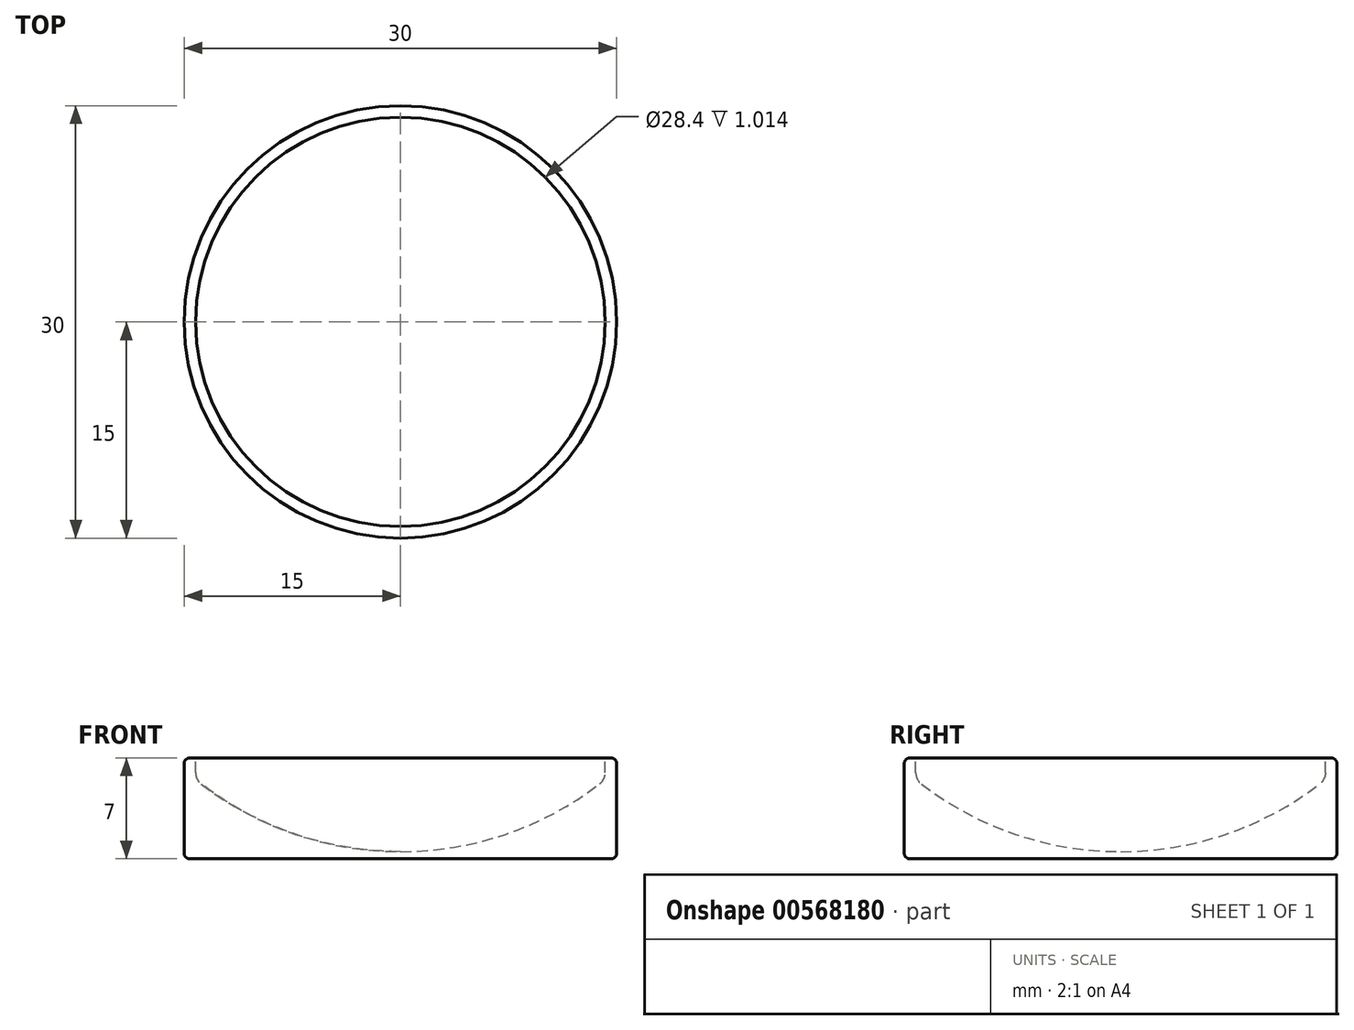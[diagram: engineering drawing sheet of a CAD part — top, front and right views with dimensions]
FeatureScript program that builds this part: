
annotation { "Feature Type Name" : "Feature", "Feature Type Description" : "" }
export const myFeature = defineFeature(function(context is Context, id is Id, definition is map)
    precondition{}
    {
        {
            var Q0;
            Q0=qCreatedBy(makeId("Front.planeOp"),FACE);
            var sketch = newSketch(context, id + "F0", { "sketchPlane" : qUnion([Q0])});
            skLineSegment(sketch, "E0", {"start": v(-15, 0) * mm, "end": v(-15, 7) * mm});
            skLineSegment(sketch, "E1", {"start": v(-15, 7) * mm, "end": v(-14.2, 7) * mm});
            skLineSegment(sketch, "E2", {"start": v(-14.2, 7) * mm, "end": v(-14.2, 5.5) * mm});
            skLineSegment(sketch, "E3", {"start": v(0, 0.5) * mm, "end": v(0, 0) * mm});
            skLineSegment(sketch, "E4", {"start": v(0, 0) * mm, "end": v(-15, 0) * mm});
            skArc(sketch, "E5", {"start": v(-14.2, 5.5) * mm, "mid": v(-7.53, 1.79) * mm, "end": v(0, 0.5) * mm});
            skSolve(sketch);
        }
        {
            var Q0;
            Q0=makeQuery(id+"F0.imprint","IMPRINT",FACE,{"disambiguationData":[TD([[makeQuery(id+"F0.imprint","IMPRINT",EDGE,{"derivedFrom":sQuery(id+"F0.wireOp",EDGE,"E0")}),-1.0]])]});
            var Q1;
            Q1=sQuery(id+"F0.wireOp",EDGE,"E3");
            revolve(context, id + "F1", {"entities" : qUnion([Q0]), "axis" : qUnion([Q1]), "revolveType" : RevolveType.FULL});
        }
        {
            var Q0;
            Q0=makeQuery(id+"F1.opRevolve","SWEPT_EDGE",EDGE,{"disambiguationData":[OSD([sQuery(id+"F0.wireOp",EDGE,"E0"),sQuery(id+"F0.wireOp",EDGE,"E1")])]});
            fillet(context, id + "F2", {"entities" : qUnion([Q0]), "radius" : 0.4 * mm, "tangentPropagation" : true, "allowEdgeOverflow" : false});
        }
        {
            var Q0;
            Q0=makeQuery(id+"F1.opRevolve","SWEPT_EDGE",EDGE,{"disambiguationData":[OSD([sQuery(id+"F0.wireOp",EDGE,"E0"),sQuery(id+"F0.wireOp",EDGE,"E4")])]});
            fillet(context, id + "F3", {"entities" : qUnion([Q0]), "radius" : 0.4 * mm, "tangentPropagation" : true, "allowEdgeOverflow" : false});
        }
        {
            var Q0;
            Q0=makeQuery(id+"F1.opRevolve","SWEPT_EDGE",EDGE,{"disambiguationData":[OSD([sQuery(id+"F0.wireOp",EDGE,"E2"),sQuery(id+"F0.wireOp",EDGE,"E5")])]});
            fillet(context, id + "F4", {"entities" : qUnion([Q0]), "radius" : 1 * mm, "tangentPropagation" : true, "allowEdgeOverflow" : false});
        }
    });
